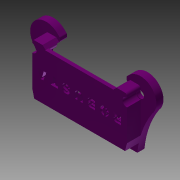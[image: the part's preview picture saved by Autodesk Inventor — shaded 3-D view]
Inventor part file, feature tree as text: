
AUTODESK INVENTOR PART (.ipt)
format: ipt  version: 2015 (Build 190159000, 159)  size: 608,768 bytes
history: native  units: mm
features: sketch x11, extrude x11, projected_geometry x5, plane x3
ambient origin geometry x8: Origin, YZ Plane, XZ Plane, XY Plane, X Axis, Y Axis, Z Axis, Center Point
bodies: Body1 (feature_tree)
feature tree (30):
  plane  "Work Plane2"
  sketch  "Sketch12"  dims[d19=46.65mm d72=0.0mm d125=-8.5mm d129=3.5mm]
  plane  "Work Plane3"
  extrude  "Extrusion9"  Depth=3.5mm
  extrude  "Extrusion10"  Depth=7.0mm TaperAngle=0.0deg
  extrude  "Extrusion11"  Depth=3.5mm TaperAngle=0.0deg
  extrude  "Extrusion12"  Depth=3.5mm TaperAngle=0.0deg
  extrude  "Extrusion13"  Depth=3.5mm TaperAngle=0.0deg
  extrude  "Extrusion14"  Depth=4.46mm
  extrude  "Extrusion15"  Depth=50.0mm TaperAngle=0.0deg
  plane  "Work Plane4"
  extrude  "Extrusion16"  Depth=7.1mm
  extrude  "Extrusion17"  Depth=7.1mm
  extrude  "Extrusion18"  Depth=50.0mm
  extrude  "Extrusion19"  [1 undecoded]
  sketch  "Sketch13"  dims[d136=-5.0mm d137=7.0mm d138=0.0mm]
  sketch  "Sketch14"  dims[d139=3.5mm d140=0.0mm d143=13.5mm d144=0.0mm]
  sketch  "Sketch16"  dims[d145=3.5mm d146=0.0mm d147=3.5mm d148=0.0mm]
  projected_geometry  "Projected Loop1"
  projected_geometry  "Projected Loop2"
  projected_geometry  "Projected Loop3"
  sketch  "Sketch17"  dims[d149=3.5mm d150=0.0mm d158=3.5mm d159=0.0mm]
  sketch  "Sketch18"  dims[d161=0.0mm d162=4.46mm]
  projected_geometry  "Projected Loop4"
  sketch  "Sketch19"  dims[d163=45.0deg d164=50.0mm d165=0.0mm]
  projected_geometry  "Projected Loop6"
  sketch  "Sketch20"  dims[d166=7.1mm d167=7.1mm]
  sketch  "Sketch21"  dims[d168=0.0mm d169=0.0mm d170=7.1mm]
  sketch  "Sketch22"  dims[d171=50.0mm d172=0.0mm d173=7.1mm]
  sketch  "Sketch25"  dims[d174=50.0mm d175=0.0mm]
note: 1 required parameter value undecoded (feature->parameter linkage not recoverable at this tier; creation-order binding heuristic only, values carry confidence <= 0.55)
